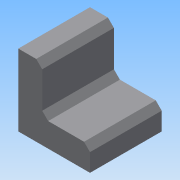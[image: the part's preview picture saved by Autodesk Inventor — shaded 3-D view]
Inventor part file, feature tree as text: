
AUTODESK INVENTOR PART (.ipt)
format: ipt  version: 2015 (Build 190159000, 159)  size: 80,384 bytes
history: native  units: in
note: dims shown in document units (in); Inventor stores cm internally (conversion verified against a paired STEP export)
features: chamfer x2, extrude x1, sketch x1
ambient origin geometry x8: Origin, YZ Plane, XZ Plane, XY Plane, X Axis, Y Axis, Z Axis, Center Point
bodies: Solid1 (feature_tree)
feature tree (4):
  extrude  "Extrusion1"  Depth=0.5in
  chamfer  "Chamfer1"  Distance=1.0in
  chamfer  "Chamfer2"  Distance=1.0in
  sketch  "Sketch1"  dims[d0=1.5in d1=0.5in d2=1.0in d3=1.0in d4=1.5in d5=0.0in d6=0.125in d7=0.125in d8=45.0deg d9=0.125in d10=0.125in d11=45.0deg]
